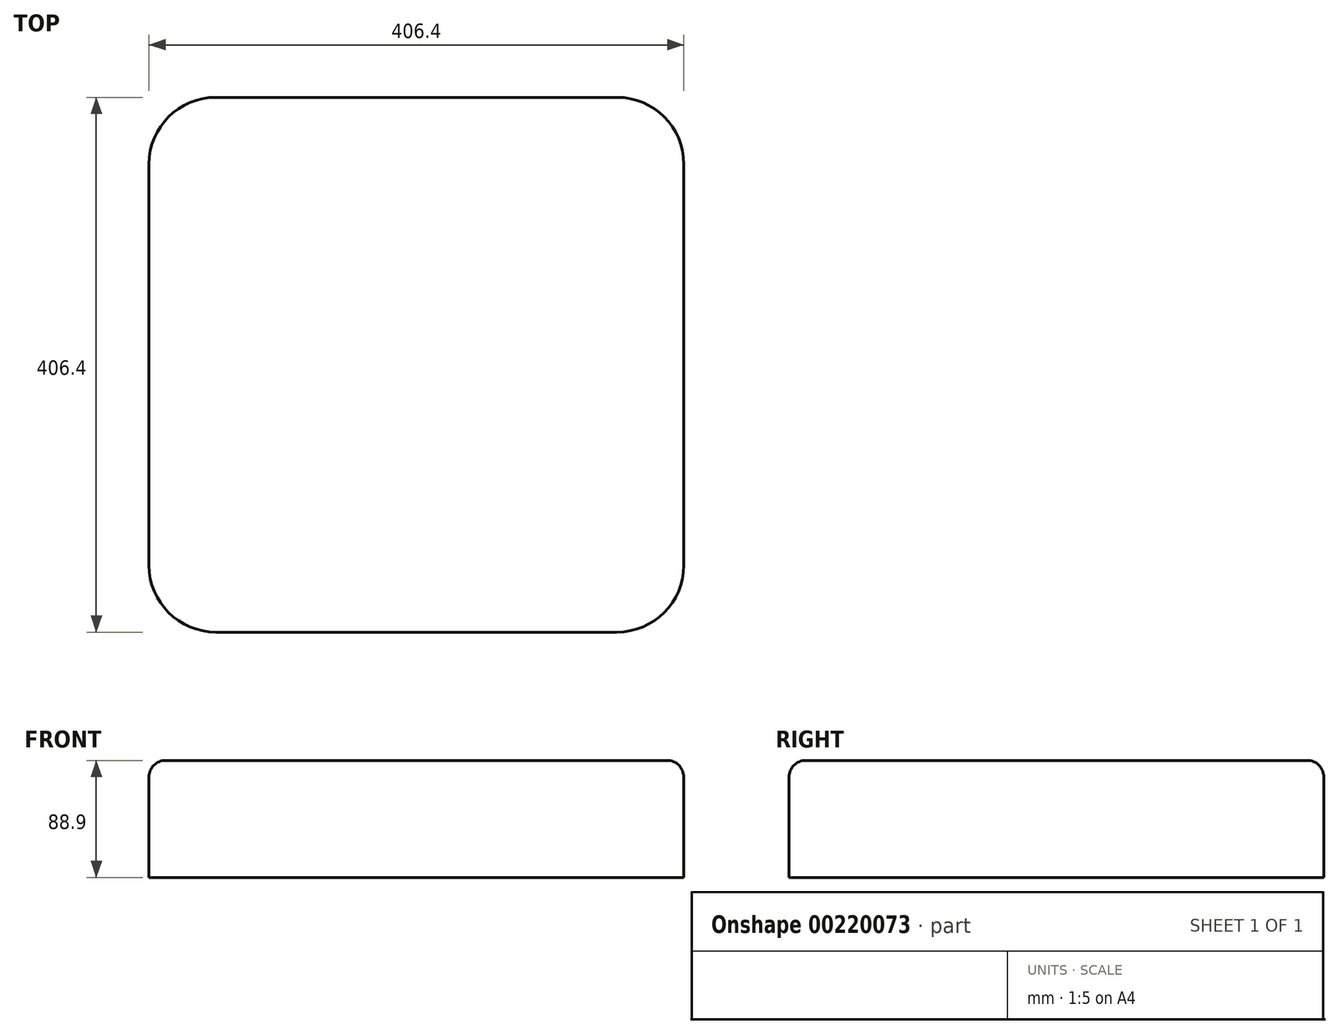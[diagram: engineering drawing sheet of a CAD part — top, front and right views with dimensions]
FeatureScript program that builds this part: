
annotation { "Feature Type Name" : "Feature", "Feature Type Description" : "" }
export const myFeature = defineFeature(function(context is Context, id is Id, definition is map)
    precondition{}
    {
        {
            var Q0;
            Q0=qCreatedBy(makeId("Top.planeOp"),FACE);
            var sketch = newSketch(context, id + "F0", { "sketchPlane" : qUnion([Q0])});
            skLineSegment(sketch, "E0.bottom", {"start": v(203.2, 203.2) * mm, "end": v(-203.2, 203.2) * mm});
            skLineSegment(sketch, "E0.top", {"start": v(203.2, -203.2) * mm, "end": v(-203.2, -203.2) * mm});
            skLineSegment(sketch, "E0.left", {"start": v(203.2, 203.2) * mm, "end": v(203.2, -203.2) * mm});
            skLineSegment(sketch, "E0.right", {"start": v(-203.2, 203.2) * mm, "end": v(-203.2, -203.2) * mm});
            skPoint(sketch, "E0.middle", {"position": v(0, 0) * mm});
            skSolve(sketch);
        }
        {
            var Q0;
            Q0 = qSketchRegion(id + "F0", true);
            extrude(context, id + "F1", {"entities" : qUnion([Q0]), "oppositeDirection" : true, "depth" : 88.9 * mm});
        }
        {
            var Q0;
            Q0=makeQuery(id+"F1.opExtrude","SWEPT_EDGE",EDGE,{"disambiguationData":[OSD([sQuery(id+"F0.wireOp",EDGE,"E0.top"),sQuery(id+"F0.wireOp",EDGE,"E0.right")])]});
            var Q1;
            Q1=makeQuery(id+"F1.opExtrude","SWEPT_EDGE",EDGE,{"disambiguationData":[OSD([sQuery(id+"F0.wireOp",EDGE,"E0.top"),sQuery(id+"F0.wireOp",EDGE,"E0.left")])]});
            var Q2;
            Q2=makeQuery(id+"F1.opExtrude","SWEPT_EDGE",EDGE,{"disambiguationData":[OSD([sQuery(id+"F0.wireOp",EDGE,"E0.bottom"),sQuery(id+"F0.wireOp",EDGE,"E0.left")])]});
            var Q3;
            Q3=makeQuery(id+"F1.opExtrude","SWEPT_EDGE",EDGE,{"disambiguationData":[OSD([sQuery(id+"F0.wireOp",EDGE,"E0.bottom"),sQuery(id+"F0.wireOp",EDGE,"E0.right")])]});
            fillet(context, id + "F2", {"entities" : qUnion([Q0, Q1, Q2, Q3]), "radius" : 50.8 * mm, "tangentPropagation" : true, "allowEdgeOverflow" : false});
        }
        {
            var Q0;
            Q0=makeQuery(id+"F1.opExtrude","CAP_EDGE",EDGE,{"disambiguationData":[OSD([sQuery(id+"F0.wireOp",EDGE,"E0.bottom")])],"isStart":true});
            fillet(context, id + "F3", {"entities" : qUnion([Q0]), "radius" : 12.7 * mm, "tangentPropagation" : true, "allowEdgeOverflow" : false});
        }
    });
